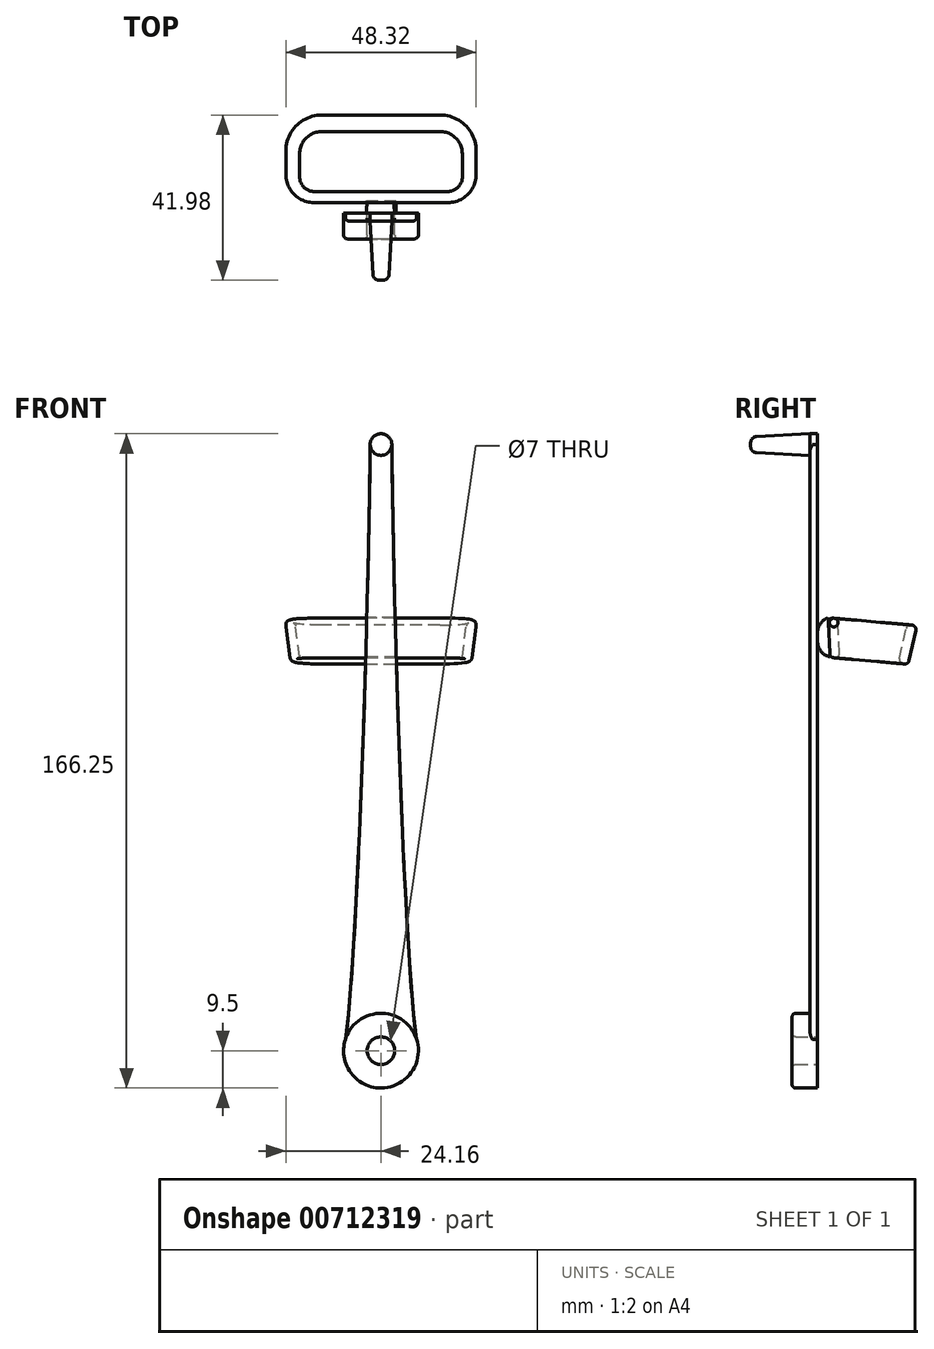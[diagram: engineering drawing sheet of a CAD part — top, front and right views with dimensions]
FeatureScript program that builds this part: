
annotation { "Feature Type Name" : "Feature", "Feature Type Description" : "" }
export const myFeature = defineFeature(function(context is Context, id is Id, definition is map)
    precondition{}
    {
        {
            var Q0;
            Q0=qCreatedBy(makeId("Front.planeOp"),FACE);
            var sketch = newSketch(context, id + "F0", { "sketchPlane" : qUnion([Q0])});
            skCircle(sketch, "E0", {"center": v(0, 0) * mm, "radius": 9.5 * mm});
            skCircle(sketch, "E1", {"center": v(0, 0) * mm, "radius": 3.5 * mm});
            skSolve(sketch);
        }
        {
            var Q0;
            Q0=makeQuery(id+"F0.imprint","IMPRINT",FACE,{"disambiguationData":[TD([[makeQuery(id+"F0.imprint","IMPRINT",EDGE,{"derivedFrom":sQuery(id+"F0.wireOp",EDGE,"E0")}),1.0]])]});
            extrude(context, id + "F1", {"entities" : qUnion([Q0]), "depth" : 4.5 * mm, "offsetDistance" : 25 * mm});
        }
        {
            var Q0;
            Q0=qCreatedBy(makeId("Front.planeOp"),FACE);
            var sketch = newSketch(context, id + "F2", { "sketchPlane" : qUnion([Q0])});
            skCircle(sketch, "E2", {"center": v(0, 154) * mm, "radius": 2.75 * mm});
            skSolve(sketch);
        }
        {
            var Q0;
            Q0=qCreatedBy(makeId("Front.planeOp"),FACE);
            var sketch = newSketch(context, id + "F3", { "sketchPlane" : qUnion([Q0])});
            skFitSpline(sketch, "E3", {"points": [v(-2.75, 154) * mm, v(-9.19, 2.27) * mm], "startDerivative": vector(-2.68, -217.9) * mm, "endDerivative": vector(-6.14, -26.1) * mm});
            skLineSegment(sketch, "E4", {"start": v(-9.19, 2.27) * mm, "end": v(0, 8.9) * mm});
            skLineSegment(sketch, "E5", {"start": v(0, 8.9) * mm, "end": v(0, 154) * mm});
            skLineSegment(sketch, "E6", {"start": v(0, 154) * mm, "end": v(-2.75, 154) * mm});
            skLineSegment(sketch, "E7.MirrorCS", {"start": v(0, 154) * mm, "end": v(2.75, 154) * mm});
            skFitSpline(sketch, "E8.MirrorCS", {"points": [v(2.75, 154) * mm, v(9.19, 2.27) * mm], "startDerivative": vector(2.68, -217.9) * mm, "endDerivative": vector(6.14, -26.1) * mm});
            skLineSegment(sketch, "E9.MirrorCS", {"start": v(9.19, 2.27) * mm, "end": v(0, 8.9) * mm});
            skSolve(sketch);
        }
        {
            var Q0;
            Q0 = qSketchRegion(id + "F3", true);
            extrude(context, id + "F4", {"entities" : qUnion([Q0]), "operationType" : NewBodyOperationType.ADD, "oppositeDirection" : true, "depth" : 2 * mm, "offsetDistance" : 25 * mm});
        }
        {
            var Q0;
            Q0 = qSketchRegion(id + "F0", true);
            extrude(context, id + "F5", {"entities" : qUnion([Q0]), "operationType" : NewBodyOperationType.ADD, "oppositeDirection" : true, "depth" : 2 * mm, "offsetDistance" : 25 * mm});
        }
        {
            var Q0;
            Q0=makeQuery(id+"F2.imprint","IMPRINT",FACE,{"disambiguationData":[TD([[makeQuery(id+"F2.imprint","IMPRINT",EDGE,{"derivedFrom":sQuery(id+"F2.wireOp",EDGE,"E2")}),1.0]])]});
            var Q1;
            Q1=sQuery(id+"F2.wireOp",EDGE,"E2");
            extrude(context, id + "F6", {"entities" : qUnion([Q0]), "operationType" : NewBodyOperationType.ADD, "surfaceEntities" : qUnion([Q1]), "depth" : 15 * mm, "offsetDistance" : 25 * mm, "hasDraft" : true, "draftAngle" : 3 * degree, "draftPullDirection" : true});
        }
        {
            var Q0;
            Q0 = qSketchRegion(id + "F2", true);
            extrude(context, id + "F7", {"entities" : qUnion([Q0]), "operationType" : NewBodyOperationType.ADD, "oppositeDirection" : true, "depth" : 2 * mm, "offsetDistance" : 25 * mm});
        }
        {
            var Q0;
            Q0=qCreatedBy(makeId("Top.planeOp"),FACE);
            cPlane(context, id + "F8", {"entities" : qUnion([Q0]), "cplaneType" : CPlaneType.OFFSET, "offset" : 100 * mm, "width" : 150 * mm, "height" : 150 * mm});
        }
        {
            var Q0;
            Q0=qCreatedBy(id+"F8.planeOp",FACE);
            var sketch = newSketch(context, id + "F9", { "sketchPlane" : qUnion([Q0])});
            skLineSegment(sketch, "E10.bottom", {"start": v(15, 23.5) * mm, "end": v(-15, 23.5) * mm});
            skLineSegment(sketch, "E10.top", {"start": v(17, 8.5) * mm, "end": v(-17, 8.5) * mm});
            skLineSegment(sketch, "E10.left", {"start": v(20.5, 18) * mm, "end": v(20.5, 12) * mm});
            skLineSegment(sketch, "E10.right", {"start": v(-20.5, 18) * mm, "end": v(-20.5, 12) * mm});
            skPoint(sketch, "E10.middle", {"position": v(0, 16) * mm});
            skPoint(sketch, "E11.visualSharp", {"position": v(-20.5, 23.5) * mm});
            skArc(sketch, "E11.filletArc", {"start": v(-15, 23.5) * mm, "mid": v(-18.89, 21.89) * mm, "end": v(-20.5, 18) * mm});
            skPoint(sketch, "E12.visualSharp", {"position": v(20.5, 23.5) * mm});
            skArc(sketch, "E12.filletArc", {"start": v(20.5, 18) * mm, "mid": v(18.89, 21.89) * mm, "end": v(15, 23.5) * mm});
            skPoint(sketch, "E13.visualSharp", {"position": v(-20.5, 8.5) * mm});
            skArc(sketch, "E13.filletArc", {"start": v(-20.5, 12) * mm, "mid": v(-19.47, 9.53) * mm, "end": v(-17, 8.5) * mm});
            skPoint(sketch, "E14.visualSharp", {"position": v(20.5, 8.5) * mm});
            skArc(sketch, "E14.filletArc", {"start": v(17, 8.5) * mm, "mid": v(19.47, 9.53) * mm, "end": v(20.5, 12) * mm});
            skArc(sketch, "E15.0", {"start": v(23, 18) * mm, "mid": v(20.66, 23.66) * mm, "end": v(15, 26) * mm});
            skLineSegment(sketch, "E15.1", {"start": v(23, 18) * mm, "end": v(23, 12) * mm});
            skLineSegment(sketch, "E15.2", {"start": v(15, 26) * mm, "end": v(-15, 26) * mm});
            skArc(sketch, "E15.3", {"start": v(17, 6) * mm, "mid": v(21.24, 7.76) * mm, "end": v(23, 12) * mm});
            skArc(sketch, "E15.4", {"start": v(-15, 26) * mm, "mid": v(-20.66, 23.66) * mm, "end": v(-23, 18) * mm});
            skLineSegment(sketch, "E15.5", {"start": v(-23, 18) * mm, "end": v(-23, 12) * mm});
            skArc(sketch, "E15.6", {"start": v(-23, 12) * mm, "mid": v(-21.24, 7.76) * mm, "end": v(-17, 6) * mm});
            skLineSegment(sketch, "E15.7", {"start": v(17, 6) * mm, "end": v(-17, 6) * mm});
            skSolve(sketch);
        }
        {
            var Q0;
            Q0=makeQuery(id+"F9.imprint","IMPRINT",FACE,{"disambiguationData":[TD([[makeQuery(id+"F9.imprint","IMPRINT",EDGE,{"derivedFrom":sQuery(id+"F9.wireOp",EDGE,"E10.bottom")}),-1.0]])]});
            extrude(context, id + "F10", {"entities" : qUnion([Q0]), "depth" : 10 * mm, "offsetDistance" : 25 * mm, "hasDraft" : true, "draftAngle" : 7.5 * degree});
        }
        {
            var Q0;
            Q0=makeQuery(id+"F9.imprint","IMPRINT",FACE,{"disambiguationData":[TD([[makeQuery(id+"F9.imprint","IMPRINT",EDGE,{"derivedFrom":sQuery(id+"F9.wireOp",EDGE,"E10.bottom")}),1.0]])]});
            extrude(context, id + "F11", {"entities" : qUnion([Q0]), "depth" : 25 * mm, "offsetDistance" : 25 * mm, "hasDraft" : true, "draftAngle" : 7.5 * degree});
        }
        {
            var Q0;
            Q0=makeQuery(id+"F11.opExtrude","SWEPT_BODY",BODY,{"disambiguationData":[OSD([sQuery(id+"F9.wireOp",EDGE,"E10.bottom"),sQuery(id+"F9.wireOp",EDGE,"E10.top"),sQuery(id+"F9.wireOp",EDGE,"E10.left"),sQuery(id+"F9.wireOp",EDGE,"E10.right"),sQuery(id+"F9.wireOp",EDGE,"E11.filletArc"),sQuery(id+"F9.wireOp",EDGE,"E12.filletArc"),sQuery(id+"F9.wireOp",EDGE,"E13.filletArc"),sQuery(id+"F9.wireOp",EDGE,"E14.filletArc")])]});
            var Q1;
            Q1=makeQuery(id+"F10.opExtrude","SWEPT_BODY",BODY,{"disambiguationData":[OSD([sQuery(id+"F9.wireOp",EDGE,"E10.bottom"),sQuery(id+"F9.wireOp",EDGE,"E10.top"),sQuery(id+"F9.wireOp",EDGE,"E10.left"),sQuery(id+"F9.wireOp",EDGE,"E10.right"),sQuery(id+"F9.wireOp",EDGE,"E11.filletArc"),sQuery(id+"F9.wireOp",EDGE,"E12.filletArc"),sQuery(id+"F9.wireOp",EDGE,"E13.filletArc"),sQuery(id+"F9.wireOp",EDGE,"E14.filletArc"),sQuery(id+"F9.wireOp",EDGE,"E15.0"),sQuery(id+"F9.wireOp",EDGE,"E15.1"),sQuery(id+"F9.wireOp",EDGE,"E15.2"),sQuery(id+"F9.wireOp",EDGE,"E15.3"),sQuery(id+"F9.wireOp",EDGE,"E15.4"),sQuery(id+"F9.wireOp",EDGE,"E15.5"),sQuery(id+"F9.wireOp",EDGE,"E15.6"),sQuery(id+"F9.wireOp",EDGE,"E15.7")])]});
            booleanBodies(context, id + "F12", {"operationType" : BooleanOperationType.SUBTRACTION, "tools" : qUnion([Q0]), "targets" : qUnion([Q1])});
        }
        {
            var Q0;
            Q0=makeQuery(id+"F7.boolean.opBoolean","MERGE",FACE,{"derivedFrom":[makeQuery(id+"F5.boolean.opBoolean","MERGE",FACE,{"derivedFrom":[makeQuery(id+"F4.opExtrude","CAP_FACE",FACE,{"disambiguationData":[OSD([sQuery(id+"F3.wireOp",EDGE,"E3"),sQuery(id+"F3.wireOp",EDGE,"E4"),sQuery(id+"F3.wireOp",EDGE,"E6"),sQuery(id+"F3.wireOp",EDGE,"E7.MirrorCS"),sQuery(id+"F3.wireOp",EDGE,"E8.MirrorCS"),sQuery(id+"F3.wireOp",EDGE,"E9.MirrorCS")])],"isStart":false}),makeQuery(id+"F5.opExtrude","CAP_FACE",FACE,{"disambiguationData":[OSD([sQuery(id+"F0.wireOp",EDGE,"E0"),sQuery(id+"F0.wireOp",EDGE,"E1")])],"isStart":false})]}),makeQuery(id+"F7.opExtrude","CAP_FACE",FACE,{"disambiguationData":[OSD([sQuery(id+"F2.wireOp",EDGE,"E2")])],"isStart":false})]});
            var sketch = newSketch(context, id + "F13", { "sketchPlane" : qUnion([Q0])});
            skLineSegment(sketch, "E16", {"start": v(-3.32, 110) * mm, "end": v(3.6, 110) * mm});
            skLineSegment(sketch, "E17", {"start": v(3.6, 110) * mm, "end": v(3.87, 100.03) * mm});
            skLineSegment(sketch, "E18", {"start": v(3.87, 100.03) * mm, "end": v(-3.87, 100.03) * mm});
            skLineSegment(sketch, "E19", {"start": v(-3.87, 100.03) * mm, "end": v(-3.32, 110) * mm});
            skSolve(sketch);
        }
        {
            var Q0;
            Q0=makeQuery(id+"F10.opExtrude","SWEPT_BODY",BODY,{"disambiguationData":[OSD([sQuery(id+"F9.wireOp",EDGE,"E10.bottom"),sQuery(id+"F9.wireOp",EDGE,"E10.top"),sQuery(id+"F9.wireOp",EDGE,"E10.left"),sQuery(id+"F9.wireOp",EDGE,"E10.right"),sQuery(id+"F9.wireOp",EDGE,"E11.filletArc"),sQuery(id+"F9.wireOp",EDGE,"E12.filletArc"),sQuery(id+"F9.wireOp",EDGE,"E13.filletArc"),sQuery(id+"F9.wireOp",EDGE,"E14.filletArc"),sQuery(id+"F9.wireOp",EDGE,"E15.0"),sQuery(id+"F9.wireOp",EDGE,"E15.1"),sQuery(id+"F9.wireOp",EDGE,"E15.2"),sQuery(id+"F9.wireOp",EDGE,"E15.3"),sQuery(id+"F9.wireOp",EDGE,"E15.4"),sQuery(id+"F9.wireOp",EDGE,"E15.5"),sQuery(id+"F9.wireOp",EDGE,"E15.6"),sQuery(id+"F9.wireOp",EDGE,"E15.7")])]});
            var Q1;
            Q1=makeQuery(id+"F10.opExtrude","CAP_EDGE",EDGE,{"disambiguationData":[OSD([sQuery(id+"F9.wireOp",EDGE,"E15.7")])],"isStart":false});
            transform(context, id + "F14", {"entities" : qUnion([Q0]), "transformType" : TransformType.ROTATION, "transformAxis" : qUnion([Q1]), "angle" : 5 * degree, "makeCopy" : false});
        }
        {
            var Q0;
            {var subQ6=sQuery(id+"F13.wireOp",EDGE,"E18");Q0=makeQuery(id+"F13.imprint","IMPRINT",FACE,{"disambiguationData":[TD([[makeQuery(id+"F13.imprint","IMPRINT",EDGE,{"derivedFrom":subQ6}),-1.0]])]});}
            var Q1;
            Q1=makeQuery(id+"F10.opExtrude","SWEPT_BODY",BODY,{"disambiguationData":[OSD([sQuery(id+"F9.wireOp",EDGE,"E10.bottom"),sQuery(id+"F9.wireOp",EDGE,"E10.top"),sQuery(id+"F9.wireOp",EDGE,"E10.left"),sQuery(id+"F9.wireOp",EDGE,"E10.right"),sQuery(id+"F9.wireOp",EDGE,"E11.filletArc"),sQuery(id+"F9.wireOp",EDGE,"E12.filletArc"),sQuery(id+"F9.wireOp",EDGE,"E13.filletArc"),sQuery(id+"F9.wireOp",EDGE,"E14.filletArc"),sQuery(id+"F9.wireOp",EDGE,"E15.0"),sQuery(id+"F9.wireOp",EDGE,"E15.1"),sQuery(id+"F9.wireOp",EDGE,"E15.2"),sQuery(id+"F9.wireOp",EDGE,"E15.3"),sQuery(id+"F9.wireOp",EDGE,"E15.4"),sQuery(id+"F9.wireOp",EDGE,"E15.5"),sQuery(id+"F9.wireOp",EDGE,"E15.6"),sQuery(id+"F9.wireOp",EDGE,"E15.7")])]});
            extrude(context, id + "F15", {"entities" : qUnion([Q0]), "endBound" : BoundingType.UP_TO_BODY, "depth" : 25 * mm, "endBoundEntityBody" : qUnion([Q1]), "offsetDistance" : 25 * mm});
        }
        {
            var Q0;
            Q0=makeQuery(id+"F15.opExtrude","CAP_EDGE",EDGE,{"disambiguationData":[OSD([sQuery(id+"F13.wireOp",EDGE,"E16")])],"isStart":true});
            var Q1;
            Q1=makeQuery(id+"F15.opExtrude","CAP_EDGE",EDGE,{"disambiguationData":[OSD([sQuery(id+"F13.wireOp",EDGE,"E18")])],"isStart":true});
            fillet(context, id + "F16", {"entities" : qUnion([Q0, Q1]), "radius" : 4 * mm, "tangentPropagation" : true, "allowEdgeOverflow" : false});
        }
        {
            var Q0;
            {var subQ0=sQuery(id+"F9.wireOp",EDGE,"E10.top");Q0=makeQuery(id+"F12.opBoolean","INTERSECT",EDGE,{"derivedFrom":[makeQuery(id+"F10.opExtrude","CAP_FACE",FACE,{"disambiguationData":[OSD([sQuery(id+"F9.wireOp",EDGE,"E10.bottom"),subQ0,sQuery(id+"F9.wireOp",EDGE,"E10.left"),sQuery(id+"F9.wireOp",EDGE,"E10.right"),sQuery(id+"F9.wireOp",EDGE,"E11.filletArc"),sQuery(id+"F9.wireOp",EDGE,"E12.filletArc"),sQuery(id+"F9.wireOp",EDGE,"E13.filletArc"),sQuery(id+"F9.wireOp",EDGE,"E14.filletArc"),sQuery(id+"F9.wireOp",EDGE,"E15.0"),sQuery(id+"F9.wireOp",EDGE,"E15.1"),sQuery(id+"F9.wireOp",EDGE,"E15.2"),sQuery(id+"F9.wireOp",EDGE,"E15.3"),sQuery(id+"F9.wireOp",EDGE,"E15.4"),sQuery(id+"F9.wireOp",EDGE,"E15.5"),sQuery(id+"F9.wireOp",EDGE,"E15.6"),sQuery(id+"F9.wireOp",EDGE,"E15.7")])],"isStart":false}),makeQuery(id+"F11.opExtrude","SWEPT_FACE",FACE,{"disambiguationData":[OSD([subQ0])]})]});}
            var Q1;
            {var subQ0=sQuery(id+"F9.wireOp",EDGE,"E10.bottom");Q1=makeQuery(id+"F12.opBoolean","MERGE",EDGE,{"derivedFrom":[makeQuery(id+"F10.opExtrude","CAP_EDGE",EDGE,{"disambiguationData":[OSD([subQ0])],"isStart":true}),makeQuery(id+"F11.opExtrude","CAP_EDGE",EDGE,{"disambiguationData":[OSD([subQ0])],"isStart":true})]});}
            var Q2;
            Q2=makeQuery(id+"F10.opExtrude","CAP_EDGE",EDGE,{"disambiguationData":[OSD([sQuery(id+"F9.wireOp",EDGE,"E15.2")])],"isStart":true});
            var Q3;
            Q3=makeQuery(id+"F10.opExtrude","CAP_EDGE",EDGE,{"disambiguationData":[OSD([sQuery(id+"F9.wireOp",EDGE,"E15.2")])],"isStart":false});
            fillet(context, id + "F17", {"entities" : qUnion([Q0, Q1, Q2, Q3]), "radius" : 1.1 * mm, "tangentPropagation" : true, "allowEdgeOverflow" : false});
        }
        {
            var Q0;
            Q0=makeQuery(id+"F6.opExtrude","CAP_EDGE",EDGE,{"disambiguationData":[OSD([sQuery(id+"F2.wireOp",EDGE,"E2")])],"isStart":false});
            fillet(context, id + "F18", {"entities" : qUnion([Q0]), "radius" : 1.5 * mm, "tangentPropagation" : true, "allowEdgeOverflow" : false});
        }
        {
            var Q0;
            Q0=makeQuery(id+"F1.opExtrude","CAP_EDGE",EDGE,{"disambiguationData":[OSD([sQuery(id+"F0.wireOp",EDGE,"E0")])],"isStart":false});
            var Q1;
            Q1=makeQuery(id+"F1.opExtrude","CAP_EDGE",EDGE,{"disambiguationData":[OSD([sQuery(id+"F0.wireOp",EDGE,"E1")])],"isStart":false});
            fillet(context, id + "F19", {"entities" : qUnion([Q0, Q1]), "radius" : 1 * mm, "tangentPropagation" : true, "allowEdgeOverflow" : false});
        }
        {
            var Q0;
            {var subQ0=sQuery(id+"F3.wireOp",EDGE,"E8.MirrorCS");Q0=makeQuery(id+"F4.boolean.opBoolean","SPLIT",EDGE,{"disambiguationData":[topologyDisambiguationEdgeConnected([makeQuery(id+"F4.opExtrude","CAP_FACE",FACE,{"disambiguationData":[OSD([sQuery(id+"F3.wireOp",EDGE,"E3"),sQuery(id+"F3.wireOp",EDGE,"E4"),sQuery(id+"F3.wireOp",EDGE,"E6"),sQuery(id+"F3.wireOp",EDGE,"E7.MirrorCS"),subQ0,sQuery(id+"F3.wireOp",EDGE,"E9.MirrorCS")])],"isStart":true})])],"derivedFrom":makeQuery(id+"F4.opExtrude","CAP_EDGE",EDGE,{"disambiguationData":[OSD([subQ0])],"isStart":true})});}
            var Q1;
            {var subQ0=sQuery(id+"F3.wireOp",EDGE,"E3");Q1=makeQuery(id+"F4.boolean.opBoolean","SPLIT",EDGE,{"disambiguationData":[topologyDisambiguationEdgeConnected([makeQuery(id+"F4.opExtrude","CAP_FACE",FACE,{"disambiguationData":[OSD([subQ0,sQuery(id+"F3.wireOp",EDGE,"E4"),sQuery(id+"F3.wireOp",EDGE,"E6"),sQuery(id+"F3.wireOp",EDGE,"E7.MirrorCS"),sQuery(id+"F3.wireOp",EDGE,"E8.MirrorCS"),sQuery(id+"F3.wireOp",EDGE,"E9.MirrorCS")])],"isStart":true})])],"derivedFrom":makeQuery(id+"F4.opExtrude","CAP_EDGE",EDGE,{"disambiguationData":[OSD([subQ0])],"isStart":true})});}
            fillet(context, id + "F20", {"entities" : qUnion([Q0, Q1]), "radius" : 0.75 * mm, "tangentPropagation" : true, "allowEdgeOverflow" : false});
        }
    });
